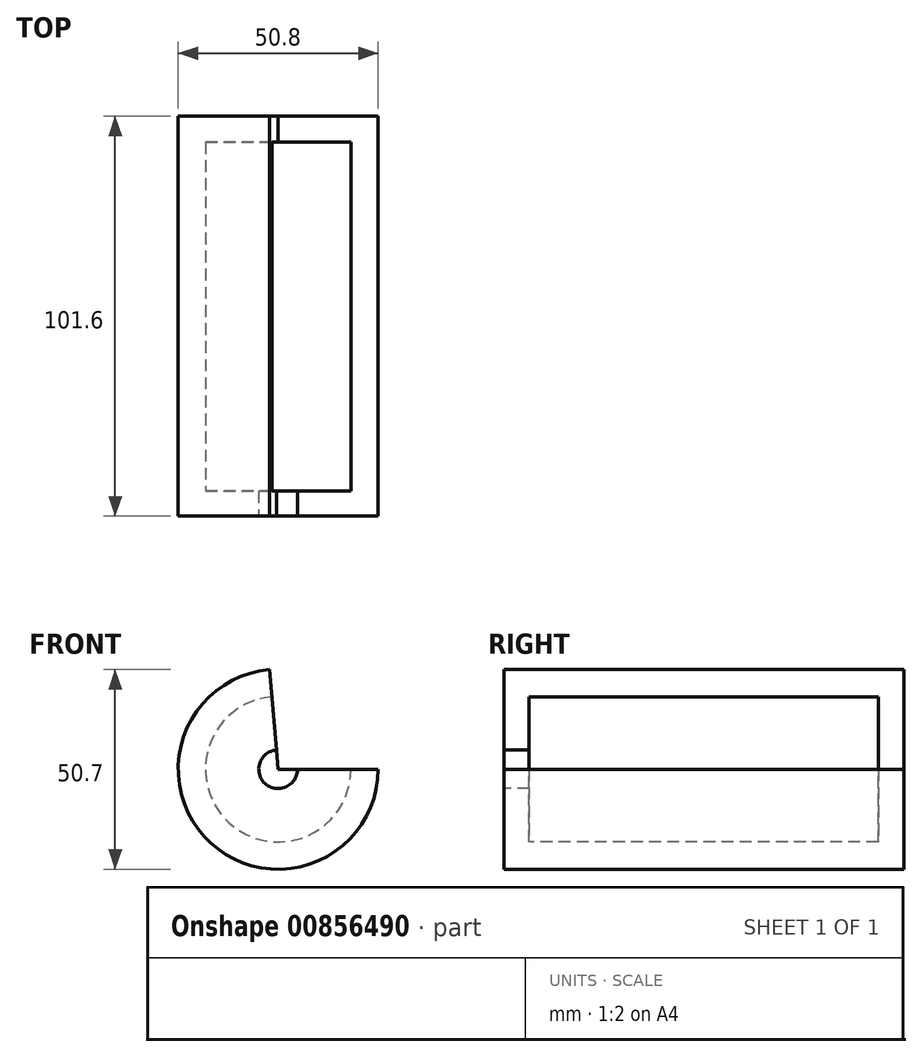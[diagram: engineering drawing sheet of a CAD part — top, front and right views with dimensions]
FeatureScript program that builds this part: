
annotation { "Feature Type Name" : "Feature", "Feature Type Description" : "" }
export const myFeature = defineFeature(function(context is Context, id is Id, definition is map)
    precondition{}
    {
        {
            var Q0;
            Q0=qCreatedBy(makeId("Top.planeOp"),FACE);
            var sketch = newSketch(context, id + "F0", { "sketchPlane" : qUnion([Q0])});
            skLineSegment(sketch, "E0", {"start": v(0, 0) * mm, "end": v(0, 50.8) * mm, "construction": true});
            skLineSegment(sketch, "E1", {"start": v(0, 0) * mm, "end": v(0, -50.8) * mm, "construction": true});
            skLineSegment(sketch, "E2", {"start": v(0, 50.8) * mm, "end": v(25.4, 50.8) * mm});
            skLineSegment(sketch, "E3", {"start": v(25.4, 50.8) * mm, "end": v(25.4, -50.8) * mm});
            skLineSegment(sketch, "E4", {"start": v(25.4, -50.8) * mm, "end": v(0, -50.8) * mm});
            skLineSegment(sketch, "E5.0", {"start": v(25.4, -44.45) * mm, "end": v(0, -44.45) * mm});
            skLineSegment(sketch, "E6", {"start": v(0, 50.8) * mm, "end": v(0, 44.25) * mm});
            skLineSegment(sketch, "E7", {"start": v(0, 44.25) * mm, "end": v(18.48, 44.25) * mm});
            skLineSegment(sketch, "E8", {"start": v(18.48, 44.25) * mm, "end": v(18.48, -44.45) * mm});
            skLineSegment(sketch, "E9", {"start": v(4.93, -44.45) * mm, "end": v(4.93, -50.8) * mm});
            skSolve(sketch);
        }
        {
            var Q0;
            {var subQ4=sQuery(id+"F0.wireOp",EDGE,"E2");Q0=makeQuery(id+"F0.imprint","IMPRINT",FACE,{"disambiguationData":[TD([[makeQuery(id+"F0.imprint","IMPRINT",EDGE,{"derivedFrom":subQ4}),-1.0]])]});}
            var Q1;
            {var subQ2=sQuery(id+"F0.wireOp",EDGE,"E9");Q1=makeQuery(id+"F0.imprint","IMPRINT",FACE,{"disambiguationData":[TD([[makeQuery(id+"F0.imprint","IMPRINT",EDGE,{"derivedFrom":subQ2}),1.0]])]});}
            var Q2;
            Q2=sQuery(id+"F0.wireOp",EDGE,"E0");
            revolve(context, id + "F1", {"surfaceOperationType" : NewSurfaceOperationType.NEW, "entities" : qUnion([Q0, Q1]), "axis" : qUnion([Q2]), "revolveType" : RevolveType.ONE_DIRECTION, "angle" : 265 * degree});
        }
    });
